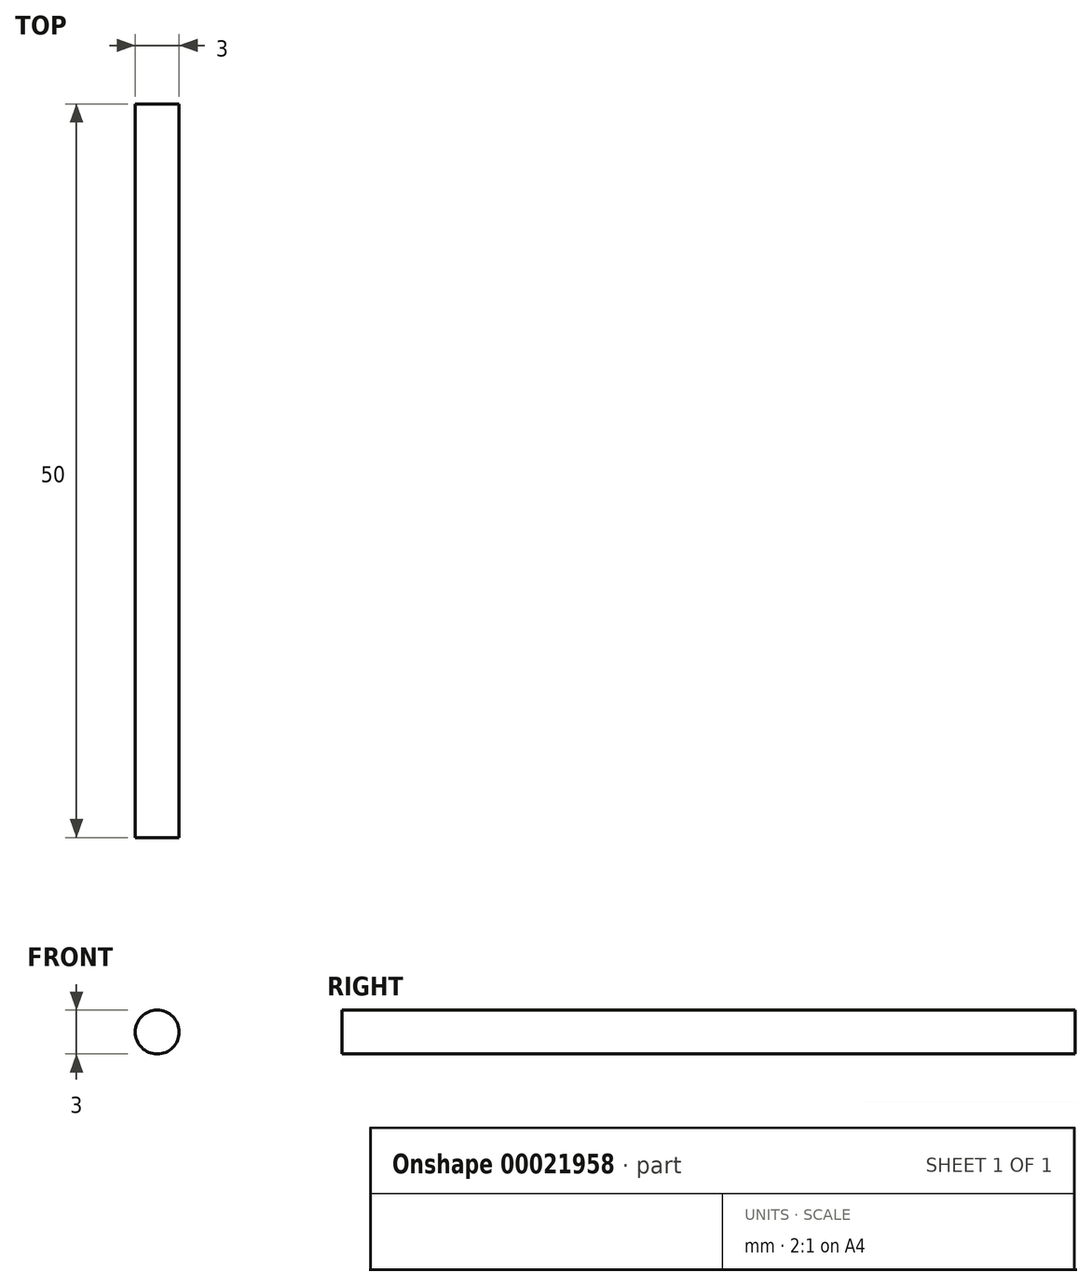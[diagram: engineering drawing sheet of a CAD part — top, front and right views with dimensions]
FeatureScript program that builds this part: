
annotation { "Feature Type Name" : "Feature", "Feature Type Description" : "" }
export const myFeature = defineFeature(function(context is Context, id is Id, definition is map)
    precondition{}
    {
        {
            var Q0;
            Q0=qCreatedBy(makeId("Front.planeOp"),FACE);
            var sketch = newSketch(context, id + "F0", { "sketchPlane" : qUnion([Q0])});
            skCircle(sketch, "E0", {"center": v(0, 0) * mm, "radius": 1.5 * mm});
            skSolve(sketch);
        }
        {
            var Q0;
            Q0 = qSketchRegion(id + "F0", true);
            extrude(context, id + "F1", {"entities" : qUnion([Q0]), "depth" : 50 * mm});
        }
    });
